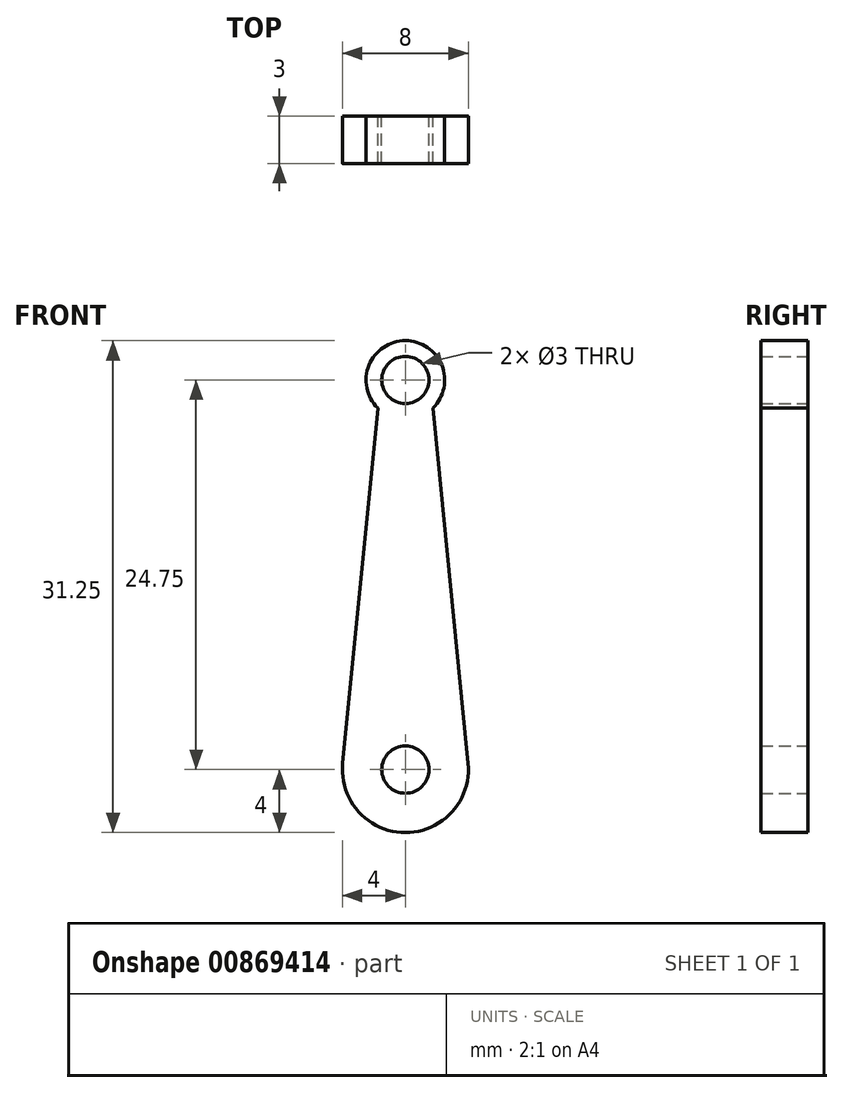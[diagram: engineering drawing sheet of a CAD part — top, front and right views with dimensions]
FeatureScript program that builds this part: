
annotation { "Feature Type Name" : "Feature", "Feature Type Description" : "" }
export const myFeature = defineFeature(function(context is Context, id is Id, definition is map)
    precondition{}
    {
        {
            var Q0;
            Q0=qCreatedBy(makeId("Front.planeOp"),FACE);
            var sketch = newSketch(context, id + "F0", { "sketchPlane" : qUnion([Q0])});
            skCircle(sketch, "E0", {"center": v(0, 0) * mm, "radius": 1.5 * mm});
            skCircle(sketch, "E1", {"center": v(0, 0) * mm, "radius": 4 * mm});
            skCircle(sketch, "E2", {"center": v(0, 24.75) * mm, "radius": 2.5 * mm});
            skLineSegment(sketch, "E3", {"start": v(-3.98, 0.4) * mm, "end": v(-1.75, 22.96) * mm});
            skLineSegment(sketch, "E4.MirrorCS", {"start": v(3.98, 0.4) * mm, "end": v(1.75, 22.96) * mm});
            skLineSegment(sketch, "E5", {"start": v(0, 24.75) * mm, "end": v(0, 0) * mm, "construction": true});
            skCircle(sketch, "E6", {"center": v(0, 24.75) * mm, "radius": 1.5 * mm});
            skSolve(sketch);
        }
        {
            var Q0;
            Q0=makeQuery(id+"F0.imprint","IMPRINT",FACE,{"disambiguationData":[TD([[makeQuery(id+"F0.imprint","IMPRINT",EDGE,{"derivedFrom":sQuery(id+"F0.wireOp",EDGE,"E0")}),-1.0]])]});
            var Q1;
            {var subQ0=sQuery(id+"F0.wireOp",EDGE,"E3");Q1=makeQuery(id+"F0.imprint","IMPRINT",FACE,{"disambiguationData":[TD([[makeQuery(id+"F0.imprint","IMPRINT",EDGE,{"derivedFrom":subQ0}),-1.0]])]});}
            var Q2;
            {var subQ0=sQuery(id+"F0.wireOp",EDGE,"E2");var subQ1=makeQuery(id+"F0.imprint","INTERSECT",VERTEX,{"derivedFrom":[subQ0,sQuery(id+"F0.wireOp",EDGE,"E3")]});Q2=makeQuery(id+"F0.imprint","IMPRINT",FACE,{"disambiguationData":[TD([[makeQuery(id+"F0.imprint","IMPRINT",EDGE,{"disambiguationData":[TD([[subQ1,-1.0]])],"derivedFrom":subQ0}),1.0]])]});}
            extrude(context, id + "F1", {"entities" : qUnion([Q0, Q1, Q2]), "endBound" : BoundingType.SYMMETRIC, "depth" : 3 * mm, "offsetDistance" : 25 * mm});
        }
    });
